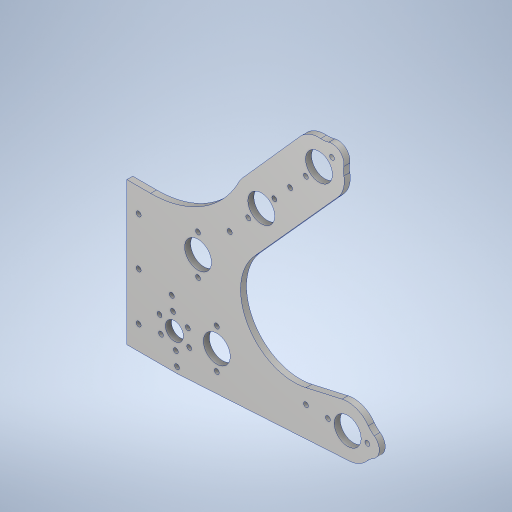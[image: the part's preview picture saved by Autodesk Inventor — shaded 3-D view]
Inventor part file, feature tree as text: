
AUTODESK INVENTOR PART (.ipt)
format: ipt  version: 2023.4 (Build 274418000, 418)  size: 379,904 bytes
history: native  units: in
note: dims shown in document units (in); Inventor stores cm internally (conversion verified against a paired STEP export)
features: sketch x2, extrude x1, hole x1, fillet x1
ambient origin geometry x8: Origin, YZ Plane, XZ Plane, XY Plane, X Axis, Y Axis, Z Axis, Center Point
bodies: Body1 (feature_tree)
feature tree (5):
  sketch  "Sketch1"  dims[d0=4.0in d2=3.0in]
  sketch  "Sketch4"  dims[d3=3.0in d4=3.0in d8=16.0in d9=12.0in d11=12.0in d13=4.5in d14=4.25in d15=0.5in d16=3.642in d17=60.0deg d63=1.125in d64=3.125in d65=1.88in d66=5.499in d67=4.018in d68=0.4688in d69=2.0in d70=0.5in d71=0.0172in d72=0.5841in d73=1.0in d74=6.0in d75=4.0in d76=1.655in d77=0.5in d79=1.0in d80=0.75in d81=1.375in d82=0.25in d83=0.0in d84=0.201in d85=0.75in d86=0.375in d87=0.25in d88=0.5635in d89=1.0in d90=0.8108in d91=1.0in d92=0.5in d93=2.3622in d95=360.0deg]
  extrude  "Extrusion2"  Depth=3.0in
  hole  "Hole2"  [1 undecoded]
  fillet  "Fillet2"  Radius=16.0in
note: 1 required parameter value undecoded (feature->parameter linkage not recoverable at this tier; creation-order binding heuristic only, values carry confidence <= 0.55)
